# Revit family: Storage-Credenza-Teknion-B_ZUL_Single_Lateral_File-R2019
name_source: partatom
category: Furniture
units: mm (PartAtom-declared; Revit-internal decimal feet)

## family parameters
Always vertical = Yes
Cut with Voids When Loaded = No
OmniClass Number = 23.40.70.14.64.21
OmniClass Title = Systems Furniture
Room Calculation Point = No
Shared = Yes
Work Plane-Based = No

## types (6) — shared parameters
Assembly Code = E2020200
Manufacturer = Teknion
Manufacturer Fax = 416.661.4586
Part Number = B_ZUL
Product Documentation Link = http://www.teknion.com
Product Line = Expansion Casegoods
Product Page URL = http://www.teknion.com
Series = Expansion Casegoods
Sustainability Data = http://www.teknion.com
URL = http://www.teknion.com
Unit Weight URL = http://www.teknion.com
Warranty = http://www.teknion.com

## per-type parameters (varying)
| type | Description | Flush, Full Modesty Panel Style | Model | Wall Access Modesty Panel Style | Worksurface Thickness |
| 1" Thick WS, Flush, Full Modesty Panel Style | Credenza with Single Lateral File, 1" Worksurface Thickness, Flush, Full Modesty Panel Style | Yes | BDZUL1________ | No | 1.016 " |
| 1" Thick WS, Wall Access Modesty Panel Style | Credenza with Single Lateral File, 1" Worksurface Thickness, Wall Access Modesty Panel Style | No | BDZUL9________ | Yes | 1.016 " |
| 1-3/16" Thick WS, Wall Access Modesty Panel Style | Credenza with Single Lateral File, 1-3/16" Worksurface Thickness, Wall Access Modesty Panel Style | No | BMZUL9________ | Yes | 1.189 " |
| 1-3/16" Thick WS, Flush, Full Modesty Panel Style | Credenza with Single Lateral File, 1-3/16" Worksurface Thickness, Flush, Full Modesty Panel Style | Yes | BMZUL1________ | No | 1.189 " |
| 1-9/16" Thick WS, Flush, Full Modesty Panel Style | Credenza with Single Lateral File, 1-9/16" Worksurface Thickness, Flush, Full Modesty Panel Style | Yes | BXZUL1________ | No | 1.555 " |
| 1-9/16" Thick WS, Wall Access Modesty Panel Style | Credenza with Single Lateral File, 1-9/16" Worksurface Thickness, Wall Access Modesty Panel Style | No | BXZUL9________ | Yes | 1.555 " |

## geometry (parser evidence)
native form markers: Blend x2, Sweep x3
no freeform markers — native parametric forms only
